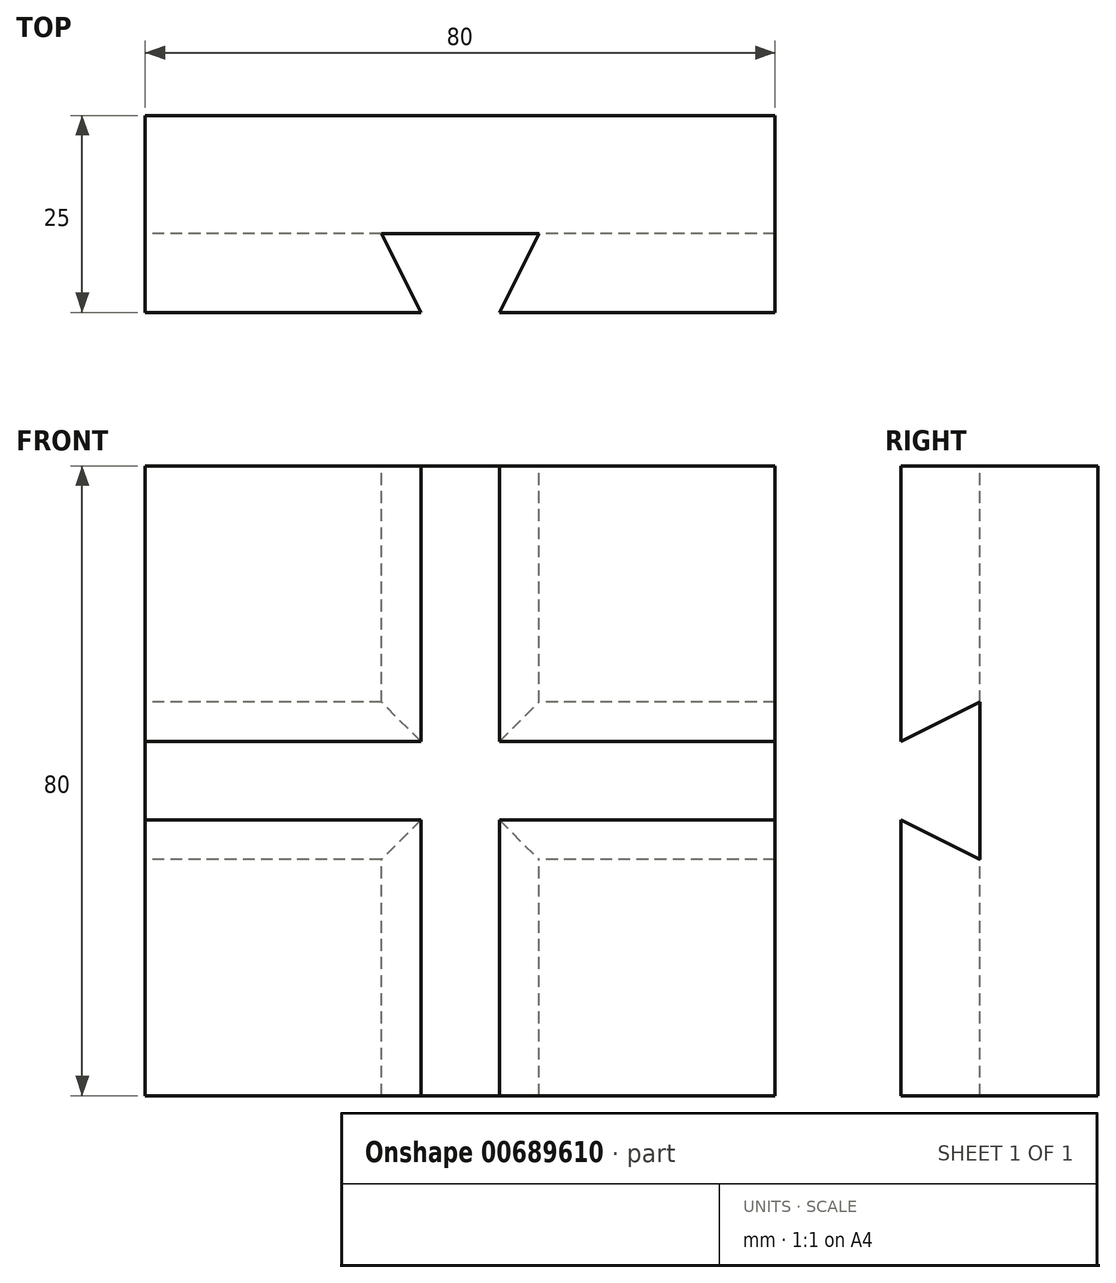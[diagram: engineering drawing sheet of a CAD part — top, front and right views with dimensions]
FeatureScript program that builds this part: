
annotation { "Feature Type Name" : "Feature", "Feature Type Description" : "" }
export const myFeature = defineFeature(function(context is Context, id is Id, definition is map)
    precondition{}
    {
        {
            var Q0;
            Q0=qCreatedBy(makeId("Front.planeOp"),FACE);
            var sketch = newSketch(context, id + "F0", { "sketchPlane" : qUnion([Q0])});
            skLineSegment(sketch, "E0.bottom", {"start": v(0, 80) * mm, "end": v(80, 80) * mm});
            skLineSegment(sketch, "E0.top", {"start": v(0, 0) * mm, "end": v(80, 0) * mm});
            skLineSegment(sketch, "E0.left", {"start": v(0, 80) * mm, "end": v(0, 0) * mm});
            skLineSegment(sketch, "E0.right", {"start": v(80, 80) * mm, "end": v(80, 0) * mm});
            skSolve(sketch);
        }
        {
            var Q0;
            Q0=makeQuery(id+"F0.imprint","IMPRINT",FACE,{"disambiguationData":[TD([[makeQuery(id+"F0.imprint","IMPRINT",EDGE,{"derivedFrom":sQuery(id+"F0.wireOp",EDGE,"E0.bottom")}),-1.0]])]});
            extrude(context, id + "F1", {"entities" : qUnion([Q0]), "depth" : 25 * mm, "offsetDistance" : 25 * mm});
        }
        {
            var Q0;
            Q0=makeQuery(id+"F1.opExtrude","SWEPT_FACE",FACE,{"disambiguationData":[OSD([sQuery(id+"F0.wireOp",EDGE,"E0.left")])]});
            var sketch = newSketch(context, id + "F2", { "sketchPlane" : qUnion([Q0])});
            skLineSegment(sketch, "E1.left", {"start": v(15, 50) * mm, "end": v(15, 30) * mm});
            skPoint(sketch, "E1.middle", {"position": v(25, 40) * mm});
            skLineSegment(sketch, "E2", {"start": v(25, 40) * mm, "end": v(25, 45) * mm});
            skLineSegment(sketch, "E3", {"start": v(25, 40) * mm, "end": v(25, 35) * mm});
            skLineSegment(sketch, "E4", {"start": v(15, 50) * mm, "end": v(25, 45) * mm});
            skLineSegment(sketch, "E5", {"start": v(15, 30) * mm, "end": v(25, 35) * mm});
            skPoint(sketch, "E1.bottom.end.orphan", {"position": v(35, 50) * mm});
            skPoint(sketch, "E1.top.end.orphan", {"position": v(35, 30) * mm});
            skSolve(sketch);
        }
        {
            var Q0;
            Q0=makeQuery(id+"F2.imprint","IMPRINT",FACE,{"disambiguationData":[TD([[makeQuery(id+"F2.imprint","IMPRINT",EDGE,{"derivedFrom":sQuery(id+"F2.wireOp",EDGE,"E1.left")}),1.0]])]});
            extrude(context, id + "F3", {"entities" : qUnion([Q0]), "operationType" : NewBodyOperationType.REMOVE, "oppositeDirection" : true, "depth" : 85 * mm, "offsetDistance" : 25 * mm});
        }
        {
            var Q0;
            Q0=makeQuery(id+"F1.opExtrude","SWEPT_FACE",FACE,{"disambiguationData":[OSD([sQuery(id+"F0.wireOp",EDGE,"E0.bottom")])]});
            var sketch = newSketch(context, id + "F4", { "sketchPlane" : qUnion([Q0])});
            skLineSegment(sketch, "E6.bottom", {"start": v(30, -15) * mm, "end": v(50, -15) * mm});
            skPoint(sketch, "E6.middle", {"position": v(40, -25) * mm});
            skLineSegment(sketch, "E7", {"start": v(40, -25) * mm, "end": v(45, -25) * mm});
            skLineSegment(sketch, "E8", {"start": v(40, -25) * mm, "end": v(35, -25) * mm});
            skLineSegment(sketch, "E9", {"start": v(50, -15) * mm, "end": v(45, -25) * mm});
            skLineSegment(sketch, "E10", {"start": v(30, -15) * mm, "end": v(35, -25) * mm});
            skPoint(sketch, "E6.right.end.orphan", {"position": v(50, -35) * mm});
            skPoint(sketch, "E6.left.end.orphan", {"position": v(30, -35) * mm});
            skSolve(sketch);
        }
        {
            var Q0;
            Q0=makeQuery(id+"F4.imprint","IMPRINT",FACE,{"disambiguationData":[TD([[makeQuery(id+"F4.imprint","IMPRINT",EDGE,{"derivedFrom":sQuery(id+"F4.wireOp",EDGE,"E6.bottom")}),-1.0]])]});
            extrude(context, id + "F5", {"entities" : qUnion([Q0]), "operationType" : NewBodyOperationType.REMOVE, "oppositeDirection" : true, "depth" : 85 * mm, "offsetDistance" : 25 * mm});
        }
    });
